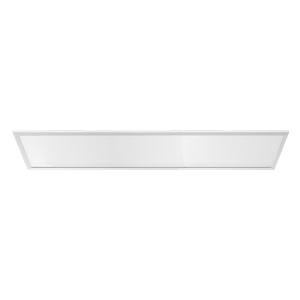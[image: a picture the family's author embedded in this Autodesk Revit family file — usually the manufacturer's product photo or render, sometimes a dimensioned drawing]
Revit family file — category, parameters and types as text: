
# Revit family: 3f_filippi_-_3f_led_panel_3f_filippi_-_22794_a01486_-_3flp30120ugr-940__1100ma____dali_4471
name_source: partatom
category: Lighting Fixtures
units: mm (PartAtom-declared; Revit-internal decimal feet)

## family parameters
Cut with Voids When Loaded = No
Host = Face
Light Source = No
Part Type = Normal
Room Calculation Point = No
Round Connector Dimension = Use Diameter
Shared = No

## types (1)
- 3F Filippi - 3F LED Panel (1 x LED, 4000 lm, 43 W, 4000 K)
    Apparent Load = 43 VA
    Approval mark = ENEC
    CIE Flux Codes = 63 88 97 100 100
    Color Rendering = 90
    Color Temperature = 4000 K
    Control Gear = Electronic transformer
    Default Elevation = 1800 mm
    Description = ILLUMINOTECHNICAL
Luminous efficiency 100% (DLOR 100%, ULOR 0%).
Initial luminous flux of the luminaire 4000 lm.
Direct symmetric distribution.
Installation Interdistance Transv.D = 1.27 x hu - Long.D = 1.18 x hu.
Average luminance <3000 cd/m² for radial angles >65°.
Tabular UGR (CIE 117 - 4H-8H; S=0.25H; 70/50/20): RUG 18.7 - 18.6.
Beam angle: 87° - 84°.
Luminous efficacy 93 lm/W.
Lifetime (L93/B10): 30000 h. (tq+25°C)
Lifetime (L90/B10): 50000 h. (tq+25°C)
Lifetime (L80/B10): 80000 h. (tq+25°C)
Lifetime (L75/B10): 100000 h. (tq+25°C)
Sudden decreased luminous flux after 50000 hours: 0% (C0).
Photobiological safety in compliance with IEC/TR 62778: RG0 risk exempt, (IEC 62471).
In compliance with IEC/EN 62722-2-1 - IEC/EN 62717 standards.

SOURCE
2 linear LED modules 940.
Energy efficiency class (UE 2019/2020 - UE 2019/2015): D.
CIE 13.3 Colour rendering index: CRI >90 (R9 >50%).
IES TM-30 Fidelity Index: Rf = 90 Rg = 98.
CCT nominal colour temperature 4000 K.
Colour initial tolerance (MacAdam): SDCM 3.

MECHANICAL
Housing in white painted epoxy-polyester powder aluminium.
Diffuser in SMP trasparent microprismatic methacrylate (PMMA) externally, anti-glare with high transmittance.
Perimetral frame in white polycarbonate.
Anti-fall safety cable.
Luminaire with limited surface temperature. - D - (EN 60598-2-24)
Dimensions: 1195x295 mm, height 9 mm. Weight 2.665 kg.
IP43 protection degree for exposed part, IP20 for recessed part.
Mechanical strength to impacts IK06 (1 joule).
Glow-wire test resistance 650°C.

ELECTRICAL
Wiring on a separate unit (Multi-current power supply, to be ordered separately).
Power of the luminaire 43 W.
CE - IEC 60598-1 - EN 60598-1.
SAFE FLICKER: PstLM=<1 and SVM=<0.4 (IEC TR 61547-1 and IEC TR 63158), to ensure a more comfortable and safe light.
Luminaire compliant with EN 60598-2-22 for power supply from a centralised emergency system CPSS (Central Power Supply System), not incorporated in the luminaire - high risk areas excluded. The default power and flux are 100% in AC and 100% in DC.
Ambient temperature from 0°C to +25°C.
Temperature class T6 max 85°C.
Relative humidity UR: <85%.

INSTALLATION
Lay-in recessed fitting / Pull-up recessed fitting with brackets / Ceiling installation with frame / Suspension via accessory.
All accessories dedicated to this product are available on the Catalog and on our website www.3F-Filippi.com.

ACCESSORIES
A01486 - DELT40C-MEL DRIVER DALI DIP-SWITCH.
DALI, PUSH-DIM, electronic wiring 230V-50/60Hz, power factor 0.95 at full load, constant output current, SELV, class II, 1 driver, 1 DALI addresse.
Multi-current power supply that allows you to choose the driving current of the fixture at the time of installation (default 900mA) according to the required illuminance.
Quick connection non-reversible plug-socket terminal block, also for cascade connection.

APPLICATIONS
Suitable product for food production plants (HACCP), IFS (Food Version 6), BRC (GSFS Food Version 7).
Environments: with VDTs, meeting rooms, offices.
Environments: recreational, transit areas, corridors, schools, stairwells.
Environments where soft diffuse light is required for optimal visual comfort.

WARNING
Luminaire designed for disposal/recycling at end-of-life.
Replaceable control gear by a professional.
    Height = 0 mm  [stored 0 ft]
    Lamp = 1 x LED
    Lamp Light Flux = 4000 lm
    Lamp Power = 43 W
    Lamp count = 1
    Length = 1195 mm
    Lifetime = 50000 h
    Luminous efficacy = 93 lm/W
    Manufacturer = 3F Filippi
    ModVariant = No
    Model = 3F Filippi - 22794+A01486 - 3FLP30120UGR-940 (1100mA) + DALI
    Mounting Place = Ceiling
    Mounting Type = Recessed
    Number of Poles = 1
    OnlyDefault = Yes
    Power Factor = 1
    Product Name = 3F Filippi - 3F LED Panel
    Product group = recessed luminaire
    ProductGroupID = 4
    Protection Class = Protection class II
    Protection Degree = IP 20
    RLX_Detail_Level = 1
    RLX_Emergency_Light_Flux = 0 lm
    RLX_Emergency_Type = 0
    RLX_Emergency_Type_DB = No
    RlxData = <blob elided: 28453 chars, md5=9e3902f5>
    Socket = socket
    Standby Power = 0 W
    System Light Flux = 4000 lm
    System Power = 43 W
    Type Comments = Product without accessories
    Type Image = 3ffilippi_3f_led_panel_300x1200.jpg
    URL = http://relux.com
    VarID = ---
    Voltage = 0 V
    Weight = 0.00 kg
    Width = 295 mm

note: [stored X ft] marks values corroborated as IEEE doubles in the binary element streams (Revit-internal decimal feet)

## geometry (parser evidence)
native form markers: Blend x4, Sweep x10
no freeform markers — native parametric forms only
